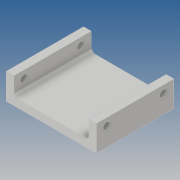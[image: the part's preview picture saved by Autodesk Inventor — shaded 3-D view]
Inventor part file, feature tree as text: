
AUTODESK INVENTOR PART (.ipt)
format: ipt  version: 2019 (Build 230136000, 136)  size: 116,224 bytes
history: native  units: mm
features: sketch x3, extrude x2, chamfer x1, hole x1
ambient origin geometry x8: Origin, YZ Plane, XZ Plane, XY Plane, X Axis, Y Axis, Z Axis, Center Point
bodies: Solide1 (feature_tree)
feature tree (7):
  extrude  "Extrusion1"  Depth=70.0mm
  extrude  "Extrusion2"  Depth=60.0mm
  chamfer  "Chanfrein1"  Distance=6.0mm
  hole  "Perçage1"  [1 undecoded]
  sketch  "Esquisse1"
  sketch  "Esquisse2"
  sketch  "Esquisse4"
note: 1 required parameter value undecoded (feature->parameter linkage not recoverable at this tier; creation-order binding heuristic only, values carry confidence <= 0.55)
